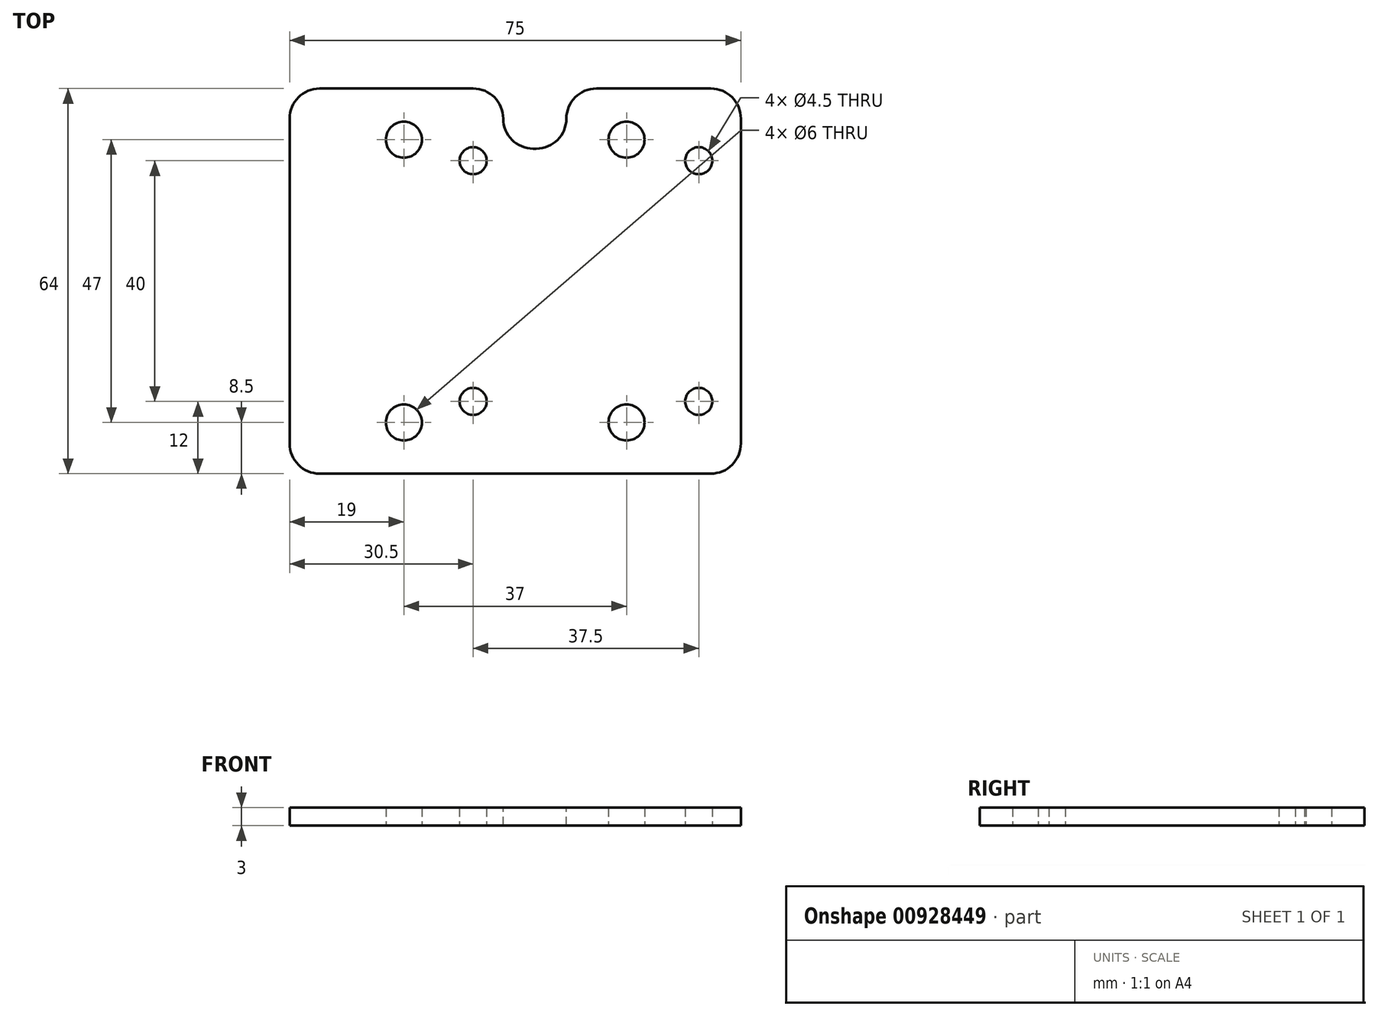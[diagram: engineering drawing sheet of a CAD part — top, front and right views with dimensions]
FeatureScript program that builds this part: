
annotation { "Feature Type Name" : "Feature", "Feature Type Description" : "" }
export const myFeature = defineFeature(function(context is Context, id is Id, definition is map)
    precondition{}
    {
        {
            var Q0;
            Q0=qCreatedBy(makeId("Top.planeOp"),FACE);
            var sketch = newSketch(context, id + "F0", { "sketchPlane" : qUnion([Q0])});
            skLineSegment(sketch, "E0.bottom", {"start": v(37.5, 20) * mm, "end": v(-37.5, 20) * mm, "construction": true});
            skLineSegment(sketch, "E0.top", {"start": v(37.5, -20) * mm, "end": v(-37.5, -20) * mm, "construction": true});
            skLineSegment(sketch, "E0.left", {"start": v(37.5, 20) * mm, "end": v(37.5, -20) * mm, "construction": true});
            skLineSegment(sketch, "E0.right", {"start": v(-37.5, 20) * mm, "end": v(-37.5, -20) * mm, "construction": true});
            skPoint(sketch, "E0.middle", {"position": v(0, 0) * mm});
            skPoint(sketch, "E1", {"position": v(0, 20) * mm});
            skPoint(sketch, "E2", {"position": v(0, -20) * mm});
            skPoint(sketch, "E3", {"position": v(45, 0) * mm});
            skLineSegment(sketch, "E4", {"start": v(0, 35) * mm, "end": v(47.5, 35) * mm, "construction": true});
            skLineSegment(sketch, "E5", {"start": v(47.5, 35) * mm, "end": v(47.5, 22.5) * mm, "construction": true});
            skLineSegment(sketch, "E6", {"start": v(47.5, 22.5) * mm, "end": v(60, 22.5) * mm});
            skLineSegment(sketch, "E7", {"start": v(60, 22.5) * mm, "end": v(60, 0) * mm});
            skLineSegment(sketch, "E8.MirrorCS", {"start": v(-60, 22.5) * mm, "end": v(-60, 0) * mm, "construction": true});
            skLineSegment(sketch, "E9.MirrorCS", {"start": v(-47.5, 22.5) * mm, "end": v(-60, 22.5) * mm, "construction": true});
            skLineSegment(sketch, "E10.MirrorCS", {"start": v(0, 35) * mm, "end": v(-47.5, 35) * mm, "construction": true});
            skLineSegment(sketch, "E11.MirrorCS", {"start": v(-47.5, 35) * mm, "end": v(-47.5, 22.5) * mm, "construction": true});
            skLineSegment(sketch, "E12.MirrorCS", {"start": v(60, 22.5) * mm, "end": v(60, 0) * mm, "construction": true});
            skLineSegment(sketch, "E13.MirrorCS", {"start": v(47.5, 22.5) * mm, "end": v(60, 22.5) * mm, "construction": true});
            skLineSegment(sketch, "E14.MirrorCS", {"start": v(60, -22.5) * mm, "end": v(60, 0) * mm, "construction": true});
            skLineSegment(sketch, "E15.MirrorCS", {"start": v(47.5, -22.5) * mm, "end": v(60, -22.5) * mm, "construction": true});
            skLineSegment(sketch, "E16.MirrorCS", {"start": v(47.5, -35) * mm, "end": v(47.5, -22.5) * mm, "construction": true});
            skLineSegment(sketch, "E17.MirrorCS", {"start": v(0, -35) * mm, "end": v(47.5, -35) * mm, "construction": true});
            skLineSegment(sketch, "E18.MirrorCS", {"start": v(0, -35) * mm, "end": v(-47.5, -35) * mm, "construction": true});
            skLineSegment(sketch, "E19.MirrorCS", {"start": v(-47.5, -35) * mm, "end": v(-47.5, -22.5) * mm, "construction": true});
            skLineSegment(sketch, "E20.MirrorCS", {"start": v(-60, -22.5) * mm, "end": v(-60, 0) * mm, "construction": true});
            skLineSegment(sketch, "E21.MirrorCS", {"start": v(-47.5, -22.5) * mm, "end": v(-60, -22.5) * mm, "construction": true});
            skPoint(sketch, "E22.MirrorP", {"position": v(-45, 0) * mm});
            skCircle(sketch, "E23", {"center": v(-37.5, 20) * mm, "radius": 2.25 * mm});
            skCircle(sketch, "E24", {"center": v(0, 20) * mm, "radius": 2.25 * mm});
            skCircle(sketch, "E25", {"center": v(37.5, 20) * mm, "radius": 2.25 * mm});
            skCircle(sketch, "E26", {"center": v(-37.5, -20) * mm, "radius": 2.25 * mm});
            skCircle(sketch, "E27", {"center": v(0, -20) * mm, "radius": 2.25 * mm});
            skCircle(sketch, "E28", {"center": v(37.5, -20) * mm, "radius": 2.25 * mm});
            skCircle(sketch, "E29", {"center": v(45, 0) * mm, "radius": 2.25 * mm});
            skCircle(sketch, "E30", {"center": v(-45, 0) * mm, "radius": 2.25 * mm});
            skSolve(sketch);
        }
        {
            var Q0;
            Q0=qCreatedBy(makeId("Top.planeOp"),FACE);
            var sketch = newSketch(context, id + "F1", { "sketchPlane" : qUnion([Q0])});
            skLineSegment(sketch, "E31.bottom", {"start": v(44.5, -32) * mm, "end": v(-30.5, -32) * mm});
            skLineSegment(sketch, "E31.top", {"start": v(44.5, 32) * mm, "end": v(-30.5, 32) * mm});
            skLineSegment(sketch, "E31.left", {"start": v(44.5, -32) * mm, "end": v(44.5, 32) * mm});
            skLineSegment(sketch, "E31.right", {"start": v(-30.5, -32) * mm, "end": v(-30.5, 32) * mm});
            skPoint(sketch, "E31.middle", {"position": v(7, 0) * mm});
            skCircle(sketch, "E32.0", {"center": v(0, 20) * mm, "radius": 2.25 * mm});
            skCircle(sketch, "E33.0", {"center": v(37.5, 20) * mm, "radius": 2.25 * mm});
            skCircle(sketch, "E34.0", {"center": v(37.5, -20) * mm, "radius": 2.25 * mm});
            skCircle(sketch, "E35.0", {"center": v(0, -20) * mm, "radius": 2.25 * mm});
            skSolve(sketch);
        }
        {
            var Q0;
            Q0 = qSketchRegion(id + "F1", true);
            extrude(context, id + "F2", {"entities" : qUnion([Q0]), "depth" : 3 * mm, "offsetDistance" : 25 * mm});
        }
        {
            var Q0;
            Q0=makeQuery(id+"F2.opExtrude","SWEPT_EDGE",EDGE,{"disambiguationData":[OSD([sQuery(id+"F1.wireOp",EDGE,"E31.top"),sQuery(id+"F1.wireOp",EDGE,"E31.right")])]});
            var Q1;
            Q1=makeQuery(id+"F2.opExtrude","SWEPT_EDGE",EDGE,{"disambiguationData":[OSD([sQuery(id+"F1.wireOp",EDGE,"E31.bottom"),sQuery(id+"F1.wireOp",EDGE,"E31.right")])]});
            var Q2;
            Q2=makeQuery(id+"F2.opExtrude","SWEPT_EDGE",EDGE,{"disambiguationData":[OSD([sQuery(id+"F1.wireOp",EDGE,"E31.bottom"),sQuery(id+"F1.wireOp",EDGE,"E31.left")])]});
            var Q3;
            Q3=makeQuery(id+"F2.opExtrude","SWEPT_EDGE",EDGE,{"disambiguationData":[OSD([sQuery(id+"F1.wireOp",EDGE,"E31.top"),sQuery(id+"F1.wireOp",EDGE,"E31.left")])]});
            fillet(context, id + "F3", {"entities" : qUnion([Q0, Q1, Q2, Q3]), "radius" : 5 * mm, "tangentPropagation" : true, "allowEdgeOverflow" : false});
        }
        {
            var Q0;
            Q0=qCreatedBy(makeId("Top.planeOp"),FACE);
            var sketch = newSketch(context, id + "F4", { "sketchPlane" : qUnion([Q0])});
            skLineSegment(sketch, "E36.bottom", {"start": v(48, -26) * mm, "end": v(-34, -26) * mm, "construction": true});
            skLineSegment(sketch, "E36.top", {"start": v(48, 26) * mm, "end": v(-34, 26) * mm, "construction": true});
            skLineSegment(sketch, "E36.left", {"start": v(48, -26) * mm, "end": v(48, 26) * mm, "construction": true});
            skLineSegment(sketch, "E36.right", {"start": v(-34, -26) * mm, "end": v(-34, 26) * mm, "construction": true});
            skPoint(sketch, "E36.middle", {"position": v(7, 0) * mm});
            skLineSegment(sketch, "E37.bottom", {"start": v(28.5, -22.5) * mm, "end": v(-14.5, -22.5) * mm, "construction": true});
            skLineSegment(sketch, "E37.top", {"start": v(28.5, 22.5) * mm, "end": v(-14.5, 22.5) * mm, "construction": true});
            skLineSegment(sketch, "E37.left", {"start": v(28.5, -22.5) * mm, "end": v(28.5, 22.5) * mm, "construction": true});
            skLineSegment(sketch, "E37.right", {"start": v(-14.5, -22.5) * mm, "end": v(-14.5, 22.5) * mm, "construction": true});
            skLineSegment(sketch, "E38.0", {"start": v(28.5, 23.5) * mm, "end": v(-14.5, 23.5) * mm, "construction": true});
            skCircle(sketch, "E39", {"center": v(25.5, 23.5) * mm, "radius": 3 * mm});
            skCircle(sketch, "E40", {"center": v(-11.5, 23.5) * mm, "radius": 3 * mm});
            skCircle(sketch, "E41.MirrorC", {"center": v(25.5, -23.5) * mm, "radius": 3 * mm});
            skCircle(sketch, "E42.MirrorC", {"center": v(-11.5, -23.5) * mm, "radius": 3 * mm});
            skSolve(sketch);
        }
        {
            var Q0;
            Q0 = qSketchRegion(id + "F4", true);
            extrude(context, id + "F5", {"entities" : qUnion([Q0]), "operationType" : NewBodyOperationType.REMOVE, "depth" : 25 * mm, "offsetDistance" : 25 * mm});
        }
        {
            var Q0;
            Q0=qCreatedBy(makeId("Top.planeOp"),FACE);
            var sketch = newSketch(context, id + "F6", { "sketchPlane" : qUnion([Q0])});
            skLineSegment(sketch, "E43.bottom", {"start": v(5, 34.99) * mm, "end": v(15.5, 34.99) * mm});
            skLineSegment(sketch, "E43.top", {"start": v(5, 22) * mm, "end": v(15.5, 22) * mm});
            skLineSegment(sketch, "E43.left", {"start": v(5, 34.99) * mm, "end": v(5, 22) * mm});
            skLineSegment(sketch, "E43.right", {"start": v(15.5, 34.99) * mm, "end": v(15.5, 22) * mm});
            skSolve(sketch);
        }
        {
            var Q0;
            Q0 = qSketchRegion(id + "F6", true);
            extrude(context, id + "F7", {"entities" : qUnion([Q0]), "operationType" : NewBodyOperationType.REMOVE, "depth" : 25 * mm, "offsetDistance" : 25 * mm});
        }
        {
            var Q0;
            Q0=makeQuery(id+"F7.boolean.opBoolean","INTERSECT",EDGE,{"derivedFrom":[makeQuery(id+"F2.opExtrude","SWEPT_FACE",FACE,{"disambiguationData":[OSD([sQuery(id+"F1.wireOp",EDGE,"E31.top")])]}),makeQuery(id+"F7.opExtrude","SWEPT_FACE",FACE,{"disambiguationData":[OSD([sQuery(id+"F6.wireOp",EDGE,"E43.left")])]})]});
            var Q1;
            Q1=makeQuery(id+"F7.boolean.opBoolean","COPY",EDGE,{"derivedFrom":makeQuery(id+"F7.opExtrude","SWEPT_EDGE",EDGE,{"disambiguationData":[OSD([sQuery(id+"F6.wireOp",EDGE,"E43.top"),sQuery(id+"F6.wireOp",EDGE,"E43.left")])]})});
            var Q2;
            Q2=makeQuery(id+"F7.boolean.opBoolean","INTERSECT",EDGE,{"derivedFrom":[makeQuery(id+"F2.opExtrude","SWEPT_FACE",FACE,{"disambiguationData":[OSD([sQuery(id+"F1.wireOp",EDGE,"E31.top")])]}),makeQuery(id+"F7.opExtrude","SWEPT_FACE",FACE,{"disambiguationData":[OSD([sQuery(id+"F6.wireOp",EDGE,"E43.right")])]})]});
            var Q3;
            Q3=makeQuery(id+"F7.boolean.opBoolean","COPY",EDGE,{"derivedFrom":makeQuery(id+"F7.opExtrude","SWEPT_EDGE",EDGE,{"disambiguationData":[OSD([sQuery(id+"F6.wireOp",EDGE,"E43.top"),sQuery(id+"F6.wireOp",EDGE,"E43.right")])]})});
            fillet(context, id + "F8", {"entities" : qUnion([Q0, Q1, Q2, Q3]), "radius" : 5 * mm, "tangentPropagation" : true, "allowEdgeOverflow" : false});
        }
    });
